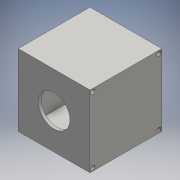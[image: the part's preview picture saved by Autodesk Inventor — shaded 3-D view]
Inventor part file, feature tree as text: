
AUTODESK INVENTOR PART (.ipt)
format: ipt  version: 2016 (Build 200138000, 138)  size: 145,920 bytes
history: native  units: mm
features: extrude x5, sketch x5
ambient origin geometry x8: Origin, YZ Plane, XZ Plane, XY Plane, X Axis, Y Axis, Z Axis, Center Point
bodies: Solid1 (feature_tree)
feature tree (10):
  extrude  "Main Block"  Depth=50.0mm
  extrude  "Motor Void"  Depth=42.0mm
  extrude  "Cable Void"  Depth=48.0mm TaperAngle=0.0deg
  extrude  "Raised Void"  Depth=4.0mm
  extrude  "Extrusion5"  Depth=50.0mm
  sketch  "Sketch1"  dims[d0=50.0mm d1=50.0mm]
  sketch  "Sketch2"  dims[d2=50.0mm d3=0.0mm d4=42.0mm]
  sketch  "Sketch3"  dims[d5=42.0mm d6=48.0mm d7=0.0mm]
  sketch  "Sketch4"  dims[d8=16.5mm d9=4.0mm]
  sketch  "Sketch5"  dims[d10=21.0mm d11=0.0mm d12=22.0mm d13=2.0mm d14=0.0mm d15=2.0mm d16=3.0mm d17=2.0mm d18=90.0deg d19=2.0mm d20=2.0mm d21=90.0deg d22=3.0mm d23=3.0mm d24=3.0mm d25=2.0mm d26=48.0mm d27=2.0mm d28=50.0mm d29=0.0mm]
